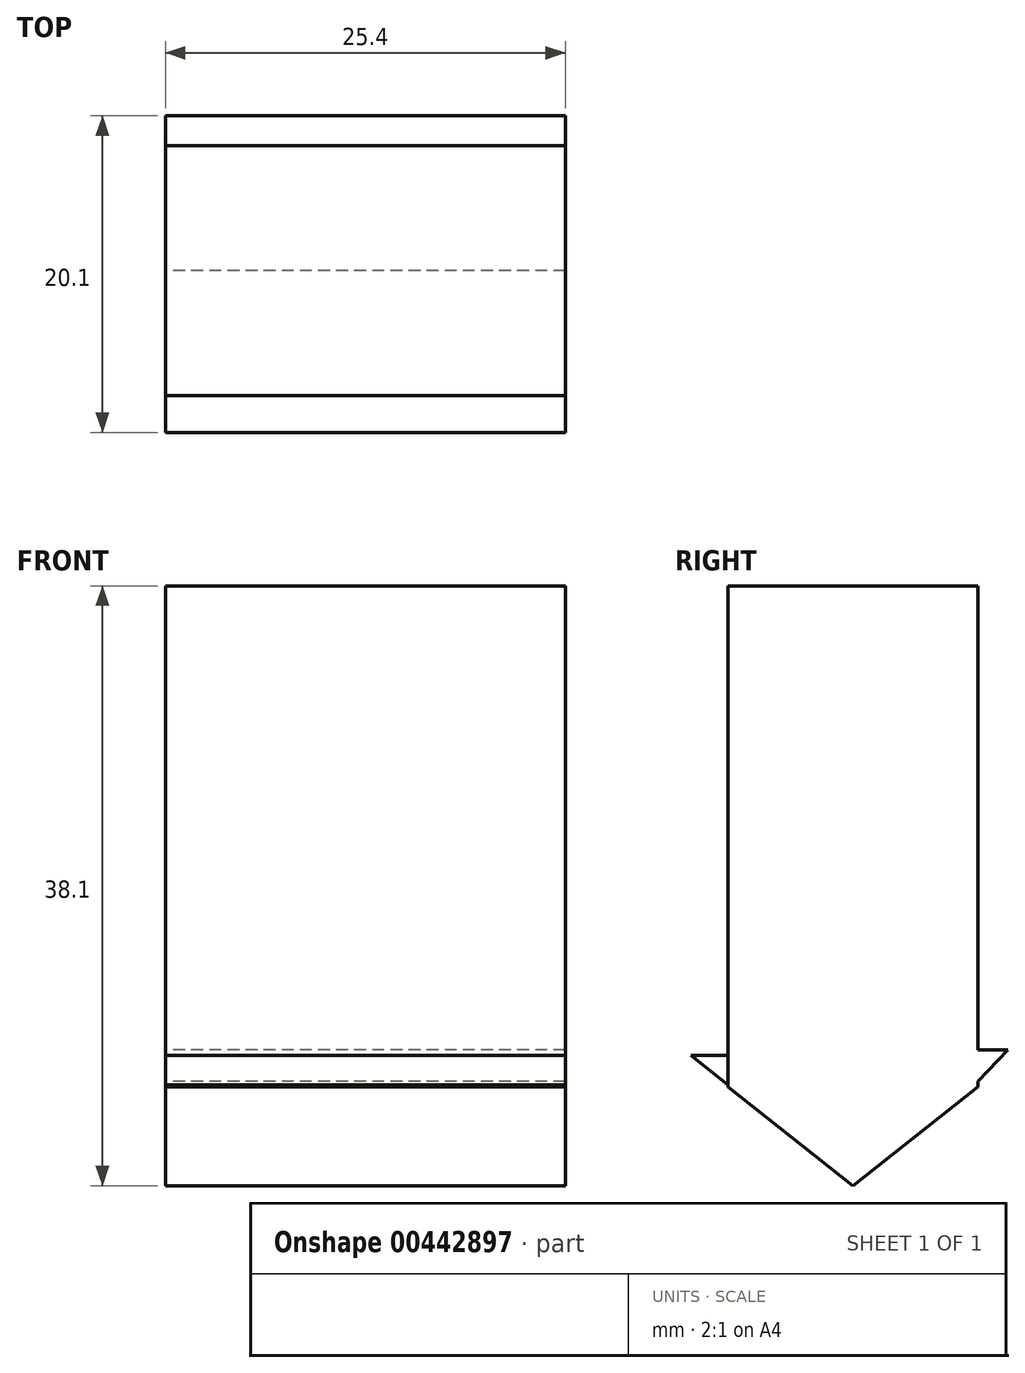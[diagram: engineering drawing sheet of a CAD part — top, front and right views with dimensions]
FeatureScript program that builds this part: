
annotation { "Feature Type Name" : "Feature", "Feature Type Description" : "" }
export const myFeature = defineFeature(function(context is Context, id is Id, definition is map)
    precondition{}
    {
        {
            var Q0;
            Q0=qCreatedBy(makeId("Front.planeOp"),FACE);
            var sketch = newSketch(context, id + "F0", { "sketchPlane" : qUnion([Q0])});
            skLineSegment(sketch, "E0.bottom", {"start": v(12.7, 19.05) * mm, "end": v(-12.7, 19.05) * mm});
            skLineSegment(sketch, "E0.top", {"start": v(12.7, -19.05) * mm, "end": v(-12.7, -19.05) * mm});
            skLineSegment(sketch, "E0.left", {"start": v(12.7, 19.05) * mm, "end": v(12.7, -19.05) * mm});
            skLineSegment(sketch, "E0.right", {"start": v(-12.7, 19.05) * mm, "end": v(-12.7, -19.05) * mm});
            skPoint(sketch, "E0.middle", {"position": v(0, 0) * mm});
            skSolve(sketch);
        }
        {
            var Q0;
            Q0=makeQuery(id+"F0.imprint","IMPRINT",FACE,{"disambiguationData":[TD([[makeQuery(id+"F0.imprint","IMPRINT",EDGE,{"derivedFrom":sQuery(id+"F0.wireOp",EDGE,"E0.bottom")}),1.0]])]});
            extrude(context, id + "F1", {"entities" : qUnion([Q0]), "depth" : 15.88 * mm});
        }
        {
            var Q0;
            Q0=makeQuery(id+"F1.opExtrude","SWEPT_FACE",FACE,{"disambiguationData":[OSD([sQuery(id+"F0.wireOp",EDGE,"E0.right")])]});
            var sketch = newSketch(context, id + "F2", { "sketchPlane" : qUnion([Q0])});
            skLineSegment(sketch, "E1", {"start": v(0, -12.95) * mm, "end": v(7.94, -19.05) * mm});
            skLineSegment(sketch, "E2", {"start": v(7.94, -19.05) * mm, "end": v(15.88, -12.79) * mm});
            skSolve(sketch);
        }
        {
            var Q0;
            {var subQ0=sQuery(id+"F2.wireOp",EDGE,"E2");Q0=makeQuery(id+"F2.imprint","IMPRINT",FACE,{"disambiguationData":[TD([[makeQuery(id+"F2.imprint","IMPRINT",EDGE,{"derivedFrom":subQ0}),-1.0]])]});}
            extrude(context, id + "F3", {"entities" : qUnion([Q0]), "operationType" : NewBodyOperationType.REMOVE, "oppositeDirection" : true, "depth" : 50.8 * mm});
        }
        {
            var Q0;
            Q0=makeQuery(id+"F1.opExtrude","SWEPT_FACE",FACE,{"disambiguationData":[OSD([sQuery(id+"F0.wireOp",EDGE,"E0.right")])]});
            var sketch = newSketch(context, id + "F4", { "sketchPlane" : qUnion([Q0])});
            skLineSegment(sketch, "E3", {"start": v(0, -12.79) * mm, "end": v(7.94, -19.05) * mm});
            skSolve(sketch);
        }
        {
            var Q0;
            {var subQ0=sQuery(id+"F4.wireOp",EDGE,"E3");Q0=makeQuery(id+"F4.imprint","IMPRINT",FACE,{"disambiguationData":[TD([[makeQuery(id+"F4.imprint","IMPRINT",EDGE,{"derivedFrom":subQ0}),-1.0]])]});}
            extrude(context, id + "F5", {"entities" : qUnion([Q0]), "operationType" : NewBodyOperationType.REMOVE, "oppositeDirection" : true, "depth" : 50.8 * mm});
        }
        {
            var Q0;
            Q0=makeQuery(id+"F1.opExtrude","SWEPT_FACE",FACE,{"disambiguationData":[OSD([sQuery(id+"F0.wireOp",EDGE,"E0.right")])]});
            var sketch = newSketch(context, id + "F6", { "sketchPlane" : qUnion([Q0])});
            skLineSegment(sketch, "E4.bottom", {"start": v(4.1, -10.5) * mm, "end": v(7.96, -10.5) * mm});
            skLineSegment(sketch, "E4.top", {"start": v(4.1, -14.63) * mm, "end": v(7.96, -14.63) * mm});
            skLineSegment(sketch, "E4.left", {"start": v(4.1, -10.5) * mm, "end": v(4.1, -14.63) * mm});
            skLineSegment(sketch, "E4.right", {"start": v(7.96, -10.5) * mm, "end": v(7.96, -14.63) * mm});
            skLineSegment(sketch, "E5.bottom", {"start": v(2.04, -10.43) * mm, "end": v(-1.9, -10.43) * mm});
            skLineSegment(sketch, "E5.top", {"start": v(2.04, -14.6) * mm, "end": v(-1.9, -14.6) * mm});
            skLineSegment(sketch, "E5.left", {"start": v(2.04, -10.43) * mm, "end": v(2.04, -14.6) * mm});
            skLineSegment(sketch, "E5.right", {"start": v(-1.9, -10.43) * mm, "end": v(-1.9, -14.6) * mm});
            skLineSegment(sketch, "E6", {"start": v(-1.9, -10.43) * mm, "end": v(2.04, -14.6) * mm});
            skLineSegment(sketch, "E7", {"start": v(7.96, -10.5) * mm, "end": v(4.1, -14.63) * mm});
            skLineSegment(sketch, "E8.bottom", {"start": v(-1.93, 2.07) * mm, "end": v(1.93, 2.07) * mm});
            skLineSegment(sketch, "E8.top", {"start": v(-1.93, -2.07) * mm, "end": v(1.93, -2.07) * mm});
            skLineSegment(sketch, "E8.left", {"start": v(-1.93, 2.07) * mm, "end": v(-1.93, -2.07) * mm});
            skLineSegment(sketch, "E8.right", {"start": v(1.93, 2.07) * mm, "end": v(1.93, -2.07) * mm});
            skLineSegment(sketch, "E9", {"start": v(1.93, 2.07) * mm, "end": v(-1.93, -2.07) * mm});
            skSolve(sketch);
        }
        {
            var Q0;
            {var subQ1=sQuery(id+"F6.wireOp",EDGE,"E4.bottom");var subQ3=makeQuery(id+"F1.opExtrude","CAP_EDGE",EDGE,{"disambiguationData":[OSD([sQuery(id+"F0.wireOp",EDGE,"E0.right")])],"isStart":false});var subQ4=makeQuery(id+"F6.imprint","INTERSECT",VERTEX,{"derivedFrom":[subQ3,subQ1]});Q0=makeQuery(id+"F6.imprint","IMPRINT",FACE,{"disambiguationData":[TD([[makeQuery(id+"F6.imprint","IMPRINT",EDGE,{"disambiguationData":[TD([[subQ4,-1.0]])],"derivedFrom":subQ3}),1.0]])]});}
            var Q1;
            {var subQ1=sQuery(id+"F6.wireOp",EDGE,"E5.bottom");var subQ3=makeQuery(id+"F1.opExtrude","CAP_EDGE",EDGE,{"disambiguationData":[OSD([sQuery(id+"F0.wireOp",EDGE,"E0.right")])],"isStart":true});var subQ4=makeQuery(id+"F6.imprint","INTERSECT",VERTEX,{"derivedFrom":[subQ3,subQ1]});Q1=makeQuery(id+"F6.imprint","IMPRINT",FACE,{"disambiguationData":[TD([[makeQuery(id+"F6.imprint","IMPRINT",EDGE,{"disambiguationData":[TD([[subQ4,-1.0]])],"derivedFrom":subQ3}),-1.0]])]});}
            extrude(context, id + "F7", {"entities" : qUnion([Q0, Q1]), "operationType" : NewBodyOperationType.ADD, "oppositeDirection" : true, "depth" : 25.4 * mm});
        }
        {
            var Q0;
            {var subQ0=sQuery(id+"F0.wireOp",EDGE,"E0.right");Q0=makeQuery(id+"F7.boolean.opBoolean","MERGE",FACE,{"derivedFrom":[makeQuery(id+"F1.opExtrude","SWEPT_FACE",FACE,{"disambiguationData":[OSD([subQ0])]}),makeQuery(id+"F7.opExtrude","CAP_FACE",FACE,{"disambiguationData":[OSD([subQ0,sQuery(id+"F6.wireOp",EDGE,"E4.bottom"),sQuery(id+"F6.wireOp",EDGE,"E7")])],"isStart":true}),makeQuery(id+"F7.opExtrude","CAP_FACE",FACE,{"disambiguationData":[OSD([subQ0,sQuery(id+"F6.wireOp",EDGE,"E5.bottom"),sQuery(id+"F6.wireOp",EDGE,"E6")])],"isStart":true})]});}
            var sketch = newSketch(context, id + "F8", { "sketchPlane" : qUnion([Q0])});
            skLineSegment(sketch, "E10.bottom", {"start": v(9.4, 12.47) * mm, "end": v(6.48, 12.47) * mm});
            skLineSegment(sketch, "E10.top", {"start": v(9.4, 17.5) * mm, "end": v(6.48, 17.5) * mm});
            skLineSegment(sketch, "E10.left", {"start": v(9.4, 12.47) * mm, "end": v(9.4, 17.5) * mm});
            skLineSegment(sketch, "E10.right", {"start": v(6.48, 12.47) * mm, "end": v(6.48, 17.5) * mm});
            skPoint(sketch, "E10.middle", {"position": v(7.94, 14.99) * mm});
            skPoint(sketch, "E10.middle.positionSnap0", {"position": v(7.94, 19.05) * mm});
            skPoint(sketch, "E10.centerSnap0", {"position": v(7.94, 19.05) * mm});
            skSolve(sketch);
        }
        {
            var Q0;
            Q0=makeQuery(id+"F8.imprint","IMPRINT",FACE,{"disambiguationData":[TD([[makeQuery(id+"F8.imprint","IMPRINT",EDGE,{"derivedFrom":sQuery(id+"F8.wireOp",EDGE,"E10.bottom")}),1.0]])]});
            var sketch = newSketch(context, id + "F9", { "sketchPlane" : qUnion([Q0])});
            skLineSegment(sketch, "E11.bottom", {"start": v(13, -10.77) * mm, "end": v(18.21, -10.77) * mm});
            skLineSegment(sketch, "E11.top", {"start": v(13, -14.96) * mm, "end": v(18.21, -14.96) * mm});
            skLineSegment(sketch, "E11.left", {"start": v(13, -10.77) * mm, "end": v(13, -14.96) * mm});
            skLineSegment(sketch, "E11.right", {"start": v(18.21, -10.77) * mm, "end": v(18.21, -14.96) * mm});
            skLineSegment(sketch, "E12", {"start": v(18.21, -10.77) * mm, "end": v(13, -14.96) * mm});
            skSolve(sketch);
        }
        {
            var Q0;
            {var subQ1=sQuery(id+"F9.wireOp",EDGE,"E11.bottom");var subQ3=makeQuery(id+"F8.imprint","IMPRINT",EDGE,{"derivedFrom":makeQuery(id+"F1.opExtrude","CAP_EDGE",EDGE,{"disambiguationData":[OSD([sQuery(id+"F0.wireOp",EDGE,"E0.right")])],"isStart":false})});var subQ4=makeQuery(id+"F9.imprint","INTERSECT",VERTEX,{"derivedFrom":[subQ3,subQ1]});Q0=makeQuery(id+"F9.imprint","IMPRINT",FACE,{"disambiguationData":[TD([[makeQuery(id+"F9.imprint","IMPRINT",EDGE,{"disambiguationData":[TD([[subQ4,-1.0]])],"derivedFrom":subQ3}),1.0]])]});}
            extrude(context, id + "F10", {"entities" : qUnion([Q0]), "oppositeDirection" : true, "depth" : 25.4 * mm});
        }
    });
